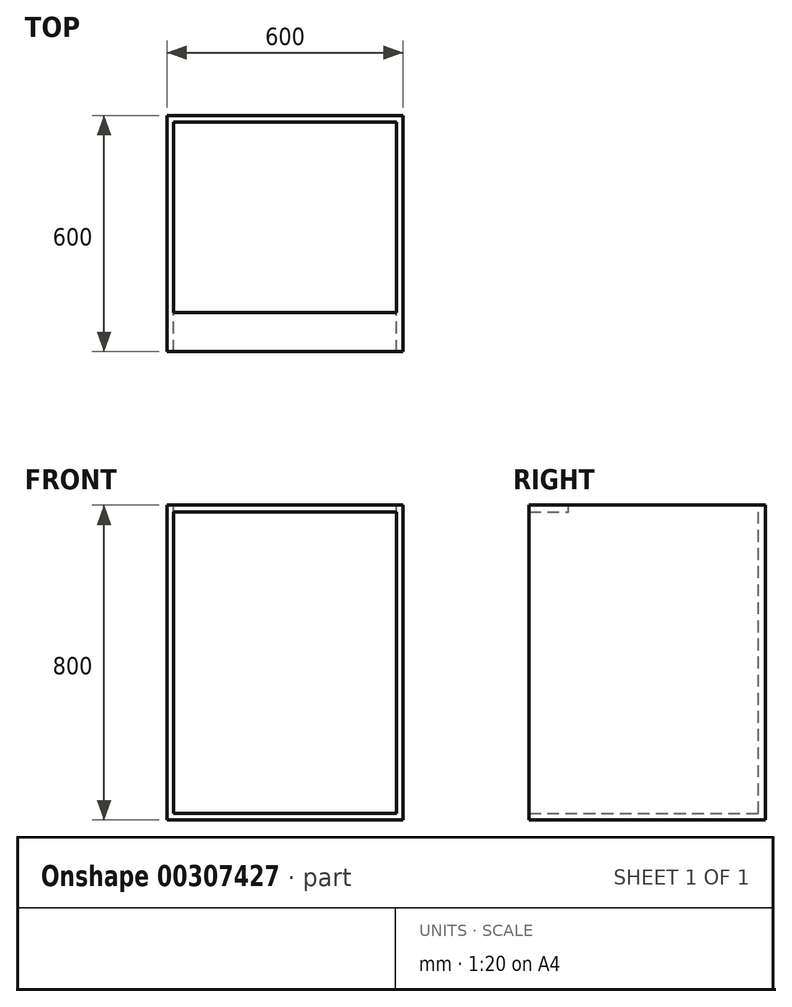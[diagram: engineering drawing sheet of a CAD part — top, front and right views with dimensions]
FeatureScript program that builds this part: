
annotation { "Feature Type Name" : "Feature", "Feature Type Description" : "" }
export const myFeature = defineFeature(function(context is Context, id is Id, definition is map)
    precondition{}
    {
        {
            var Q0;
            Q0=qCreatedBy(makeId("Front.planeOp"),FACE);
            var sketch = newSketch(context, id + "F0", { "sketchPlane" : qUnion([Q0])});
            skLineSegment(sketch, "E0.bottom", {"start": v(0, 0) * mm, "end": v(600, 0) * mm});
            skLineSegment(sketch, "E0.top", {"start": v(0, 800) * mm, "end": v(600, 800) * mm});
            skLineSegment(sketch, "E0.left", {"start": v(0, 0) * mm, "end": v(0, 800) * mm});
            skLineSegment(sketch, "E0.right", {"start": v(600, 0) * mm, "end": v(600, 800) * mm});
            skSolve(sketch);
        }
        {
            var Q0;
            Q0=makeQuery(id+"F0.imprint","IMPRINT",FACE,{"disambiguationData":[TD([[makeQuery(id+"F0.imprint","IMPRINT",EDGE,{"derivedFrom":sQuery(id+"F0.wireOp",EDGE,"E0.bottom")}),1.0]])]});
            extrude(context, id + "F1", {"entities" : qUnion([Q0]), "depth" : 600 * mm, "offsetDistance" : 25 * mm});
        }
        {
            var Q0;
            Q0=makeQuery(id+"F1.opExtrude","CAP_FACE",FACE,{"disambiguationData":[OSD([sQuery(id+"F0.wireOp",EDGE,"E0.bottom"),sQuery(id+"F0.wireOp",EDGE,"E0.top"),sQuery(id+"F0.wireOp",EDGE,"E0.left"),sQuery(id+"F0.wireOp",EDGE,"E0.right")])],"isStart":false});
            shell(context, id + "F2", {"entities" : qUnion([Q0]), "thickness" : 17 * mm});
        }
        {
            var Q0;
            Q0=makeQuery(id+"F1.opExtrude","CAP_FACE",FACE,{"disambiguationData":[OSD([sQuery(id+"F0.wireOp",EDGE,"E0.bottom"),sQuery(id+"F0.wireOp",EDGE,"E0.top"),sQuery(id+"F0.wireOp",EDGE,"E0.left"),sQuery(id+"F0.wireOp",EDGE,"E0.right")])],"isStart":false});
            var sketch = newSketch(context, id + "F3", { "sketchPlane" : qUnion([Q0])});
            skLineSegment(sketch, "E1.0", {"start": v(0, 800) * mm, "end": v(600, 800) * mm});
            skLineSegment(sketch, "E2.0", {"start": v(0, 0) * mm, "end": v(0, 800) * mm});
            skLineSegment(sketch, "E3.0", {"start": v(600, 0) * mm, "end": v(600, 800) * mm});
            skSolve(sketch);
        }
        {
            var Q0;
            Q0=makeQuery(id+"F1.opExtrude","SWEPT_FACE",FACE,{"disambiguationData":[OSD([sQuery(id+"F0.wireOp",EDGE,"E0.top")])]});
            var sketch = newSketch(context, id + "F4", { "sketchPlane" : qUnion([Q0])});
            skLineSegment(sketch, "E4.0.1", {"start": v(17, -600) * mm, "end": v(583, -600) * mm});
            skLineSegment(sketch, "E4.0.3", {"start": v(583, -600) * mm, "end": v(17, -600) * mm});
            skLineSegment(sketch, "E5.0", {"start": v(17, -17) * mm, "end": v(583, -17) * mm});
            skLineSegment(sketch, "E6.0", {"start": v(17, -600) * mm, "end": v(17, -17) * mm});
            skLineSegment(sketch, "E7.0", {"start": v(583, -600) * mm, "end": v(583, -17) * mm});
            skLineSegment(sketch, "E8", {"start": v(583, -500) * mm, "end": v(17, -500) * mm});
            skSolve(sketch);
        }
        {
            var Q0;
            {var subQ0=sQuery(id+"F4.wireOp",EDGE,"E5.0");Q0=makeQuery(id+"F4.imprint","IMPRINT",FACE,{"disambiguationData":[TD([[makeQuery(id+"F4.imprint","IMPRINT",EDGE,{"derivedFrom":subQ0}),-1.0]])]});}
            extrude(context, id + "F5", {"entities" : qUnion([Q0]), "operationType" : NewBodyOperationType.REMOVE, "endBound" : BoundingType.UP_TO_NEXT, "oppositeDirection" : true, "depth" : 25 * mm, "offsetDistance" : 25 * mm});
        }
    });
